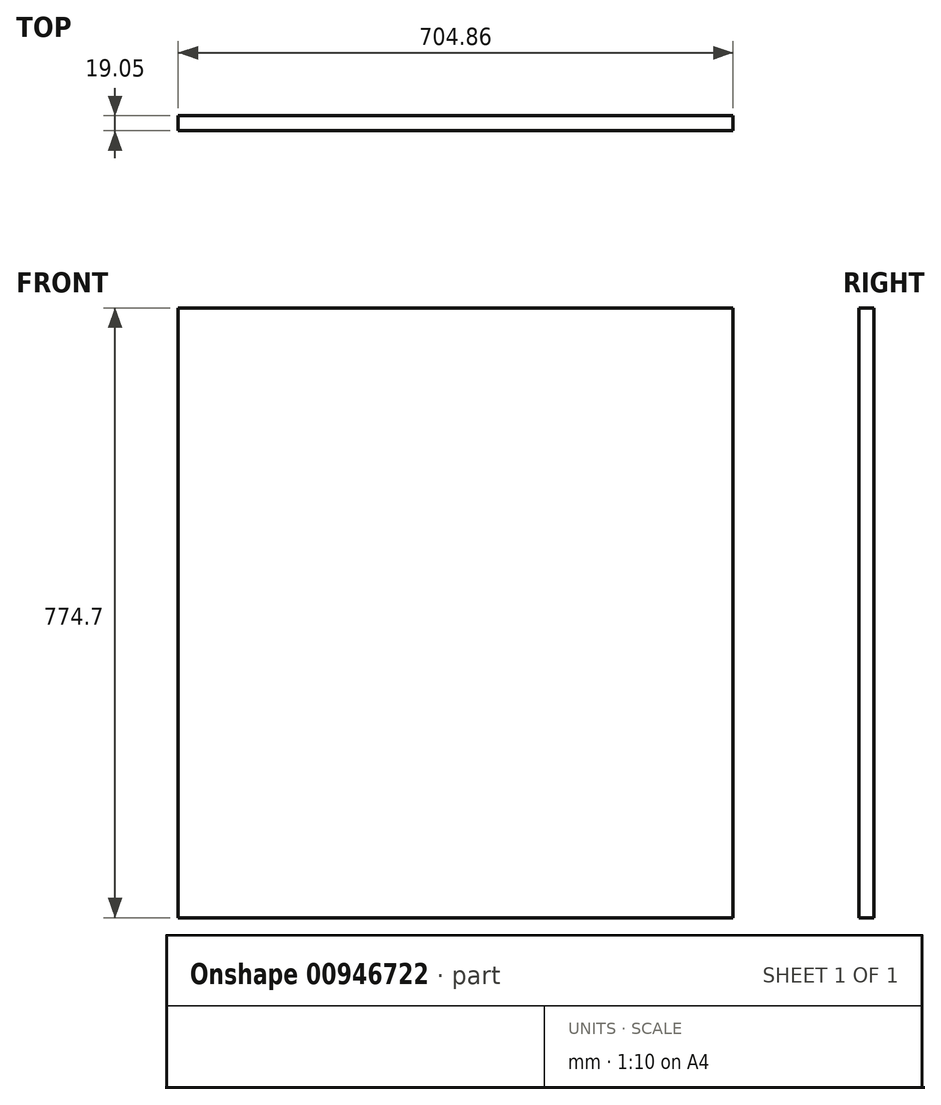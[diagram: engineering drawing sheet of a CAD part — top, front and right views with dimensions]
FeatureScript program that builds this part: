
annotation { "Feature Type Name" : "Feature", "Feature Type Description" : "" }
export const myFeature = defineFeature(function(context is Context, id is Id, definition is map)
    precondition{}
    {
        {
            var Q0;
            Q0=qCreatedBy(makeId("Front.planeOp"),FACE);
            var sketch = newSketch(context, id + "F0", { "sketchPlane" : qUnion([Q0])});
            skLineSegment(sketch, "E0.bottom", {"start": v(352.43, 387.35) * mm, "end": v(-352.43, 387.35) * mm});
            skLineSegment(sketch, "E0.top", {"start": v(352.43, -387.35) * mm, "end": v(-352.43, -387.35) * mm});
            skLineSegment(sketch, "E0.left", {"start": v(352.43, 387.35) * mm, "end": v(352.43, -387.35) * mm});
            skLineSegment(sketch, "E0.right", {"start": v(-352.43, 387.35) * mm, "end": v(-352.43, -387.35) * mm});
            skPoint(sketch, "E0.middle", {"position": v(0, 0) * mm});
            skSolve(sketch);
        }
        {
            var Q0;
            Q0=makeQuery(id+"F0.imprint","IMPRINT",FACE,{"disambiguationData":[TD([[makeQuery(id+"F0.imprint","IMPRINT",EDGE,{"derivedFrom":sQuery(id+"F0.wireOp",EDGE,"E0.bottom")}),1.0]])]});
            extrude(context, id + "F1", {"entities" : qUnion([Q0]), "depth" : 19.05 * mm, "offsetDistance" : 25.4 * mm});
        }
    });
